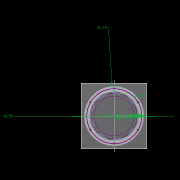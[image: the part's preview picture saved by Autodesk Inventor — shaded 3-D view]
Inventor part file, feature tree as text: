
AUTODESK INVENTOR PART (.ipt)
format: ipt  version: 2022.2 (Build 262287010, 287A)  size: 530,432 bytes
history: native  units: mm
features: other x19, extrude x19, sketch x12, pattern_circular x9, plane x3, fillet x2, move_body x2, revolve x2, draft x2, chamfer x2
ambient origin geometry x8: Origin, YZ Plane, XZ Plane, XY Plane, X Axis, Y Axis, Z Axis, Center Point
bodies: Solid5 (feature_tree)
feature tree (72):
  other  "CrossSection1"
  sketch  "Sketch7"  dims[d90=61.984365mm]
  other  "Roller1"
  other  "Roller2"
  sketch  "Sketch22"  dims[d167=8.972256mm]
  sketch  "Sketch2"  dims[d57=4.025mm]
  sketch  "Sketch23"  dims[d173=10.814812mm]
  other  "RevRoller1"
  fillet  "Fillet1"  Radius=59.246882mm
  pattern_circular  "Circular Pattern13"  Count=360  [1 undecoded]
  move_body  "Move Body7"
  revolve  "Revolution13"  [1 undecoded]
  fillet  "Fillet3"  Radius=0.025mm
  pattern_circular  "Circular Pattern14"  [2 undecoded]
  move_body  "Move Body6"
  revolve  "Revolution14"  [1 undecoded]
  other  "OuterRim_Top2"
  other  "OuterRim_Bottom2"
  plane  "Work Plane7"
  sketch  "Sketch47"  dims[d349=47.575591mm]
  sketch  "Sketch48"  dims[d350=47.575427mm]
  extrude  "Extrusion39"  Depth=5.596758mm
  extrude  "Extrusion40"  Depth=5.596758mm
  pattern_circular  "Circular Pattern28"  Angle=360.0deg  [1 undecoded]
  sketch  "Sketch49"  dims[d351=0.025mm d352=0.025mm d354=0.1mm d355=16.1595mm d356=16.159664mm d358=360.0deg d359=0.5mm d360=240.0mm d361=360.0deg d363=1.308997mm d367=8.1mm d370=0.1mm d371=1.0mm d372=1.308997mm d373=90.0deg d374=0.5mm d375=240.0mm d376=360.0deg d378=90.0deg d379=0.1mm d380=0.1mm d381=0.1mm d382=0.1mm d383=0.1mm d384=11.193516mm d385=0.0mm d386=0.0mm d391=50.0mm d392=75.0mm d393=1.5mm d394=1.5mm d395=1.5mm d396=1.5mm d397=90.0deg d398=90.0deg d399=90.0deg d400=75.0mm d401=11.193516mm d402=0.0mm d486=0.436332mm d487=0.5mm d488=2.0mm d489=0.0mm d490=20.0mm d495=2.5mm d496=8.0mm d506=13.856406mm d507=55.5mm d508=8.0mm d509=0.05mm d510=2.5mm d511=30.0deg d512=12.0mm d513=6.0mm d514=0.2mm d515=30.0deg d516=131.0mm d517=65.5mm d518=0.2mm d519=100.0mm d520=120.0mm d521=2.0mm d522=150.0mm d530=50.0mm d531=5.5mm d532=5.5mm d533=5.5mm d534=85.75mm d535=73.5mm d536=61.25mm d537=24.5mm d538=3.0mm d539=2.4mm d540=0.0mm d541=0.0mm d542=0.0mm d543=5.5mm d544=3.0mm d545=0.0mm d546=90.0mm d547=360.0deg d549=3.0mm d550=3.0mm d551=2.4mm d552=0.0mm d553=5.596758mm d554=0.0mm d555=2.4mm d556=0.0mm d557=5.596758mm d558=0.0mm d559=5.596758mm d560=0.0mm d561=90.0mm d562=360.0deg d564=60.0mm d565=360.0deg d567=5.5mm d568=5.5mm d569=3.0mm d570=0.0mm d571=5.596758mm d572=0.0mm d573=3.0mm d574=0.0mm d575=5.596758mm d576=0.0mm d577=90.0mm d578=360.0deg d580=60.0mm d581=360.0deg d584=20.0mm d585=8.0mm d587=1.75mm d589=3.0mm d592=2.0mm d593=12.0mm d594=12.0mm d600=0.5mm d601=2.0mm d602=45.0deg d603=0.5mm d604=2.0mm d605=45.0deg d606=0.436332mm d607=0.5mm d608=0.0mm d609=20.0mm d611=360.0deg d613=0.0mm d614=0.0mm d617=0.99971mm d618=100.0mm d620=69.0mm d621=3.0mm d622=5.5mm d623=5.596758mm d624=0.0mm d625=3.0mm d626=0.0mm d627=60.0mm d628=360.0deg d630=5.5mm d631=3.0mm d632=5.596758mm d633=0.0mm d634=2.593516mm d635=0.0mm d636=60.0mm d637=360.0deg d16=0.872665mm d17=0.872665mm d49=0.872665mm d50=0.872665mm d51=0.872665mm d52=0.872665mm d236=0.5mm d237=0.872665mm d238=0.5mm d239=0.872665mm d282=1.0mm d283=1.0mm d284=1.0mm d285=0.15mm d286=0.25mm d287=0.375mm d288=14.3117mm d289=0.75mm d290=20.594885mm d291=0.0625mm d292=0.75mm d293=0.375mm d405=0.5mm d406=0.872665mm d407=0.5mm d408=0.872665mm d413=0.5mm d414=0.872665mm d415=0.5mm d416=0.872665mm d417=0.5mm d418=0.872665mm d419=0.5mm d420=0.872665mm d421=0.872665mm d431=0.5mm d432=0.872665mm d433=0.5mm d434=0.872665mm d471=0.5mm d472=0.872665mm d473=0.5mm d474=0.872665mm d497=0.5mm d498=0.872665mm d499=0.5mm d500=0.872665mm d590=0.5mm d591=0.872665mm]
  extrude  "Extrusion41"  Depth=5.596758mm
  extrude  "Extrusion42"  Depth=5.596758mm
  pattern_circular  "Circular Pattern29"  Angle=360.0deg  [1 undecoded]
  extrude  "Rotor_Ring"  Depth=5.596758mm
  draft  "FaceDraft2"
  sketch  "Sketch30"  dims[d201=75.0mm d232=0.0mm d233=3600.0mm]
  plane  "Work Plane5"
  other  "Rotor Featurs"
  other  "RotorRim_Bottom"
  extrude  "Extrusion24"  Depth=5.596758mm
  extrude  "Extrusion25"  Depth=0.1mm
  extrude  "Extrusion26"  Depth=5.596758mm
  pattern_circular  "Circular Pattern23"  [2 undecoded]
  sketch  "Sketch41"  dims[d346=0.025mm]
  extrude  "Extrusion27"  TaperAngle=90.0deg  [1 undecoded]
  extrude  "Extrusion28"  Depth=5.596758mm
  pattern_circular  "Circular Pattern24"  Count=24  [1 undecoded]
  extrude  "Extrusion29"  TaperAngle=360.0deg  [1 undecoded]
  extrude  "Extrusion30"  TaperAngle=90.0deg  [1 undecoded]
  extrude  "Extrusion31"  Depth=0.1mm
  pattern_circular  "Circular Pattern25"  [2 undecoded]
  sketch  "Sketch42"  dims[d347=0.1mm]
  extrude  "Extrusion32"  Depth=0.1mm
  extrude  "Extrusion33"  Depth=0.1mm
  extrude  "Extrusion34"  Depth=0.1mm
  extrude  "Extrusion35"  Depth=5.596758mm
  pattern_circular  "Circular Pattern26"  [2 undecoded]
  pattern_circular  "Circular Pattern27"  [2 undecoded]
  chamfer  "Chamfer1"  Distance=50.0mm
  chamfer  "Chamfer2"  Distance=75.0mm
  draft  "FaceDraft4"
  plane  "Work Plane6"
  sketch  "Sketch43"  dims[d348=0.1mm]
  extrude  "Extrusion37"  Depth=1.5mm
  extrude  "Extrusion38"  Depth=1.5mm
  other  "2D Equation Curve1"
  sketch  "Sketch40"  dims[d343=16.1595mm d344=16.159664mm d345=0.025mm]
  other  "Work Axis6"
  other  "Work Axis7"
  other  "Work Axis8"
  other  "Work Axis9"
  other  "Work Axis10"
  other  "Work Point1"
  other  "Work Point2"
  other  "Work Point3"
  other  "Work Point4"
  other  "Work Point5"
note: 19 required parameter values undecoded (feature->parameter linkage not recoverable at this tier; creation-order binding heuristic only, values carry confidence <= 0.55)